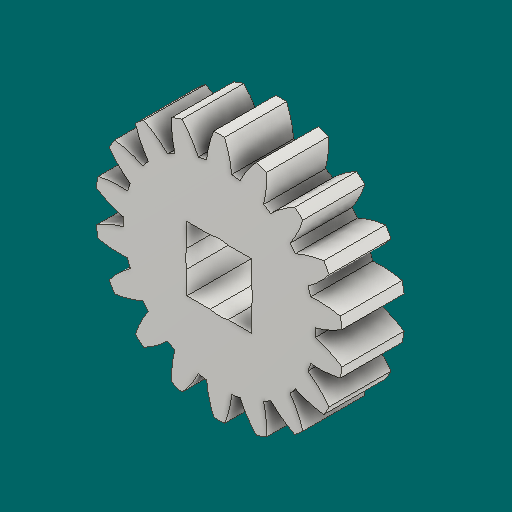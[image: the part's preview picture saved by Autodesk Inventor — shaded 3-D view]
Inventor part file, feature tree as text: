
AUTODESK INVENTOR PART (.ipt)
format: ipt  version: 2023.1 (Build 271208000, 208)  size: 335,872 bytes
history: native  units: mm (DEFAULTED — no unit token found)
features: sketch x4, extrude x3, plane x3, other x3, chamfer x1, projected_geometry x1
ambient origin geometry x8: Origin, YZ Plane, XZ Plane, XY Plane, X Axis, Y Axis, Z Axis, Center Point
bodies: Solid1 (feature_tree)
feature tree (15):
  extrude  "Extrusion1"  Depth=6.35mm TaperAngle=0.0deg
  plane  "Work Plane1"
  plane  "Work Plane2"
  plane  "Work Plane3"
  other  "Spur Gear"
  extrude  "Extrusion2"  Depth=76.2mm TaperAngle=0.0deg
  extrude  "Extrusion3"  TaperAngle=0.0deg  [1 undecoded]
  chamfer  "Chamfer1"  Distance=22.86mm
  sketch  "Sketch1"  dims[d0=25.4mm d1=6.35mm d2=0.0mm]
  sketch  "Sketch2"  dims[d3=22.86mm d4=76.2mm d5=0.0mm]
  other  "Srf1"
  sketch  "Sketch3"  dims[d6=0.0mm d7=1.745329mm d9=0.0mm]
  sketch  "Sketch4"  dims[d14=0.0mm d15=22.86mm d16=0.0mm d17=0.0mm d18=0.0mm d19=22.86mm d20=6.604mm d21=6.604mm d22=6.858mm d23=0.0mm d24=0.0mm d25=12.7mm d26=1.2mm d27=0.0mm d28=0.6mm d29=3.175mm d30=45.0deg]
  projected_geometry  "Projected Loop1"
  other  "Pitch Diameter"
note: 1 required parameter value undecoded (feature->parameter linkage not recoverable at this tier; creation-order binding heuristic only, values carry confidence <= 0.55)
